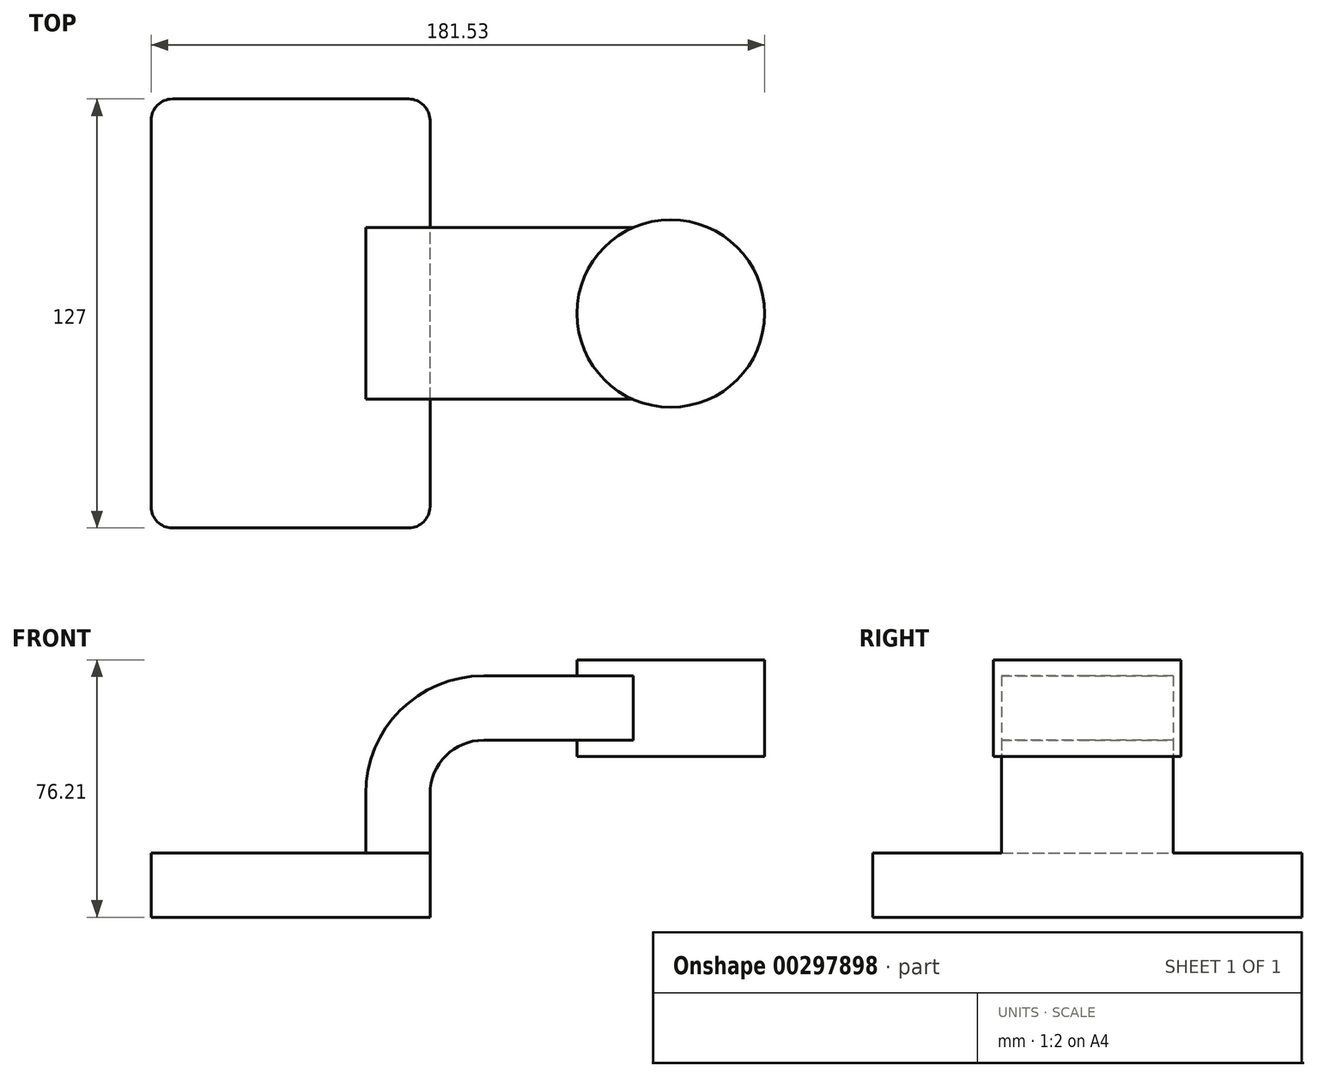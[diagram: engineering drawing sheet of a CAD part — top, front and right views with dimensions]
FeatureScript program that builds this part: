
annotation { "Feature Type Name" : "Feature", "Feature Type Description" : "" }
export const myFeature = defineFeature(function(context is Context, id is Id, definition is map)
    precondition{}
    {
        {
            var Q0;
            Q0=qCreatedBy(makeId("Front.planeOp"),FACE);
            var sketch = newSketch(context, id + "F0", { "sketchPlane" : qUnion([Q0])});
            skLineSegment(sketch, "E0.bottom", {"start": v(-41.27, -9.53) * mm, "end": v(41.28, -9.53) * mm});
            skLineSegment(sketch, "E0.top", {"start": v(-41.28, 9.52) * mm, "end": v(41.28, 9.52) * mm});
            skLineSegment(sketch, "E0.left", {"start": v(-41.28, -9.53) * mm, "end": v(-41.28, 9.52) * mm});
            skLineSegment(sketch, "E0.right", {"start": v(41.28, -9.53) * mm, "end": v(41.28, 9.52) * mm});
            skPoint(sketch, "E0.middle", {"position": v(0, 0) * mm});
            skLineSegment(sketch, "E1.bottom", {"start": v(140.26, 66.68) * mm, "end": v(89.46, 66.68) * mm});
            skLineSegment(sketch, "E1.top", {"start": v(140.26, 38.1) * mm, "end": v(89.46, 38.1) * mm});
            skLineSegment(sketch, "E1.left", {"start": v(140.26, 66.68) * mm, "end": v(140.26, 38.1) * mm});
            skLineSegment(sketch, "E1.right", {"start": v(89.46, 66.68) * mm, "end": v(89.46, 38.1) * mm});
            skPoint(sketch, "E1.middle", {"position": v(114.86, 52.39) * mm});
            skLineSegment(sketch, "E2", {"start": v(41.27, 9.52) * mm, "end": v(41.27, 27) * mm});
            skArc(sketch, "E3", {"start": v(41.27, 27) * mm, "mid": v(45.92, 38.23) * mm, "end": v(57.15, 42.88) * mm});
            skLineSegment(sketch, "E4", {"start": v(57.15, 42.88) * mm, "end": v(112.51, 42.88) * mm});
            skLineSegment(sketch, "E5.0", {"start": v(57.15, 61.93) * mm, "end": v(112.51, 61.93) * mm});
            skArc(sketch, "E5.1", {"start": v(22.22, 27) * mm, "mid": v(32.45, 51.7) * mm, "end": v(57.15, 61.93) * mm});
            skLineSegment(sketch, "E5.2", {"start": v(22.22, 9.52) * mm, "end": v(22.22, 27) * mm});
            skLineSegment(sketch, "E6", {"start": v(112.51, 38.1) * mm, "end": v(112.51, 66.68) * mm});
            skPoint(sketch, "E6.startSnap0", {"position": v(114.86, 38.1) * mm});
            skPoint(sketch, "E7.2.internal.snap0", {"position": v(32.45, 51.7) * mm});
            skFitSpline(sketch, "E8", {"points": [v(-41.27, 9.52) * mm, v(57.15, 61.93) * mm], "startDerivative": vector(45, 119.56) * mm, "endDerivative": vector(120.02, -23.13) * mm});
            skSolve(sketch);
        }
        {
            var Q0;
            Q0=makeQuery(id+"F0.imprint","IMPRINT",FACE,{"disambiguationData":[TD([[makeQuery(id+"F0.imprint","IMPRINT",EDGE,{"derivedFrom":sQuery(id+"F0.wireOp",EDGE,"E0.bottom")}),1.0]])]});
            extrude(context, id + "F1", {"entities" : qUnion([Q0]), "endBound" : BoundingType.SYMMETRIC, "depth" : 127 * mm});
        }
        {
            var Q0;
            {var subQ1=sQuery(id+"F0.wireOp",EDGE,"E2");Q0=makeQuery(id+"F0.imprint","IMPRINT",FACE,{"disambiguationData":[TD([[makeQuery(id+"F0.imprint","IMPRINT",EDGE,{"derivedFrom":subQ1}),1.0]])]});}
            var Q1;
            {var subQ0=sQuery(id+"F0.wireOp",EDGE,"E5.0");var subQ1=sQuery(id+"F0.wireOp",EDGE,"E1.right");var subQ2=makeQuery(id+"F0.imprint","INTERSECT",VERTEX,{"derivedFrom":[subQ1,subQ0]});Q1=makeQuery(id+"F0.imprint","IMPRINT",FACE,{"disambiguationData":[TD([[makeQuery(id+"F0.imprint","IMPRINT",EDGE,{"disambiguationData":[TD([[subQ2,-1.0]])],"derivedFrom":subQ1}),1.0]])]});}
            extrude(context, id + "F2", {"entities" : qUnion([Q0, Q1]), "operationType" : NewBodyOperationType.ADD, "endBound" : BoundingType.SYMMETRIC, "depth" : 50.8 * mm});
        }
        {
            var Q0;
            Q0=makeQuery(id+"F0.imprint","IMPRINT",FACE,{"disambiguationData":[TD([[makeQuery(id+"F0.imprint","IMPRINT",EDGE,{"derivedFrom":sQuery(id+"F0.wireOp",EDGE,"E5.1")}),1.0]])]});
            extrude(context, id + "F3", {"entities" : qUnion([Q0]), "operationType" : NewBodyOperationType.ADD, "endBound" : BoundingType.SYMMETRIC, "depth" : 15.88 * mm});
        }
        {
            var Q0;
            {var subQ4=sQuery(id+"F0.wireOp",EDGE,"E1.left");Q0=makeQuery(id+"F0.imprint","IMPRINT",FACE,{"disambiguationData":[TD([[makeQuery(id+"F0.imprint","IMPRINT",EDGE,{"derivedFrom":subQ4}),-1.0]])]});}
            var Q1;
            Q1=sQuery(id+"F0.wireOp",EDGE,"E6");
            revolve(context, id + "F4", {"operationType" : NewBodyOperationType.ADD, "entities" : qUnion([Q0]), "axis" : qUnion([Q1]), "revolveType" : RevolveType.FULL});
        }
        {
            var Q0;
            Q0=makeQuery(id+"F1.opExtrude","CAP_EDGE",EDGE,{"disambiguationData":[OSD([sQuery(id+"F0.wireOp",EDGE,"E0.left")])],"isStart":false});
            var Q1;
            Q1=makeQuery(id+"F1.opExtrude","CAP_EDGE",EDGE,{"disambiguationData":[OSD([sQuery(id+"F0.wireOp",EDGE,"E0.right")])],"isStart":false});
            var Q2;
            Q2=makeQuery(id+"F1.opExtrude","CAP_EDGE",EDGE,{"disambiguationData":[OSD([sQuery(id+"F0.wireOp",EDGE,"E0.right")])],"isStart":true});
            var Q3;
            Q3=makeQuery(id+"F1.opExtrude","CAP_EDGE",EDGE,{"disambiguationData":[OSD([sQuery(id+"F0.wireOp",EDGE,"E0.left")])],"isStart":true});
            fillet(context, id + "F5", {"entities" : qUnion([Q0, Q1, Q2, Q3]), "radius" : 6.35 * mm, "tangentPropagation" : true, "allowEdgeOverflow" : false});
        }
    });
